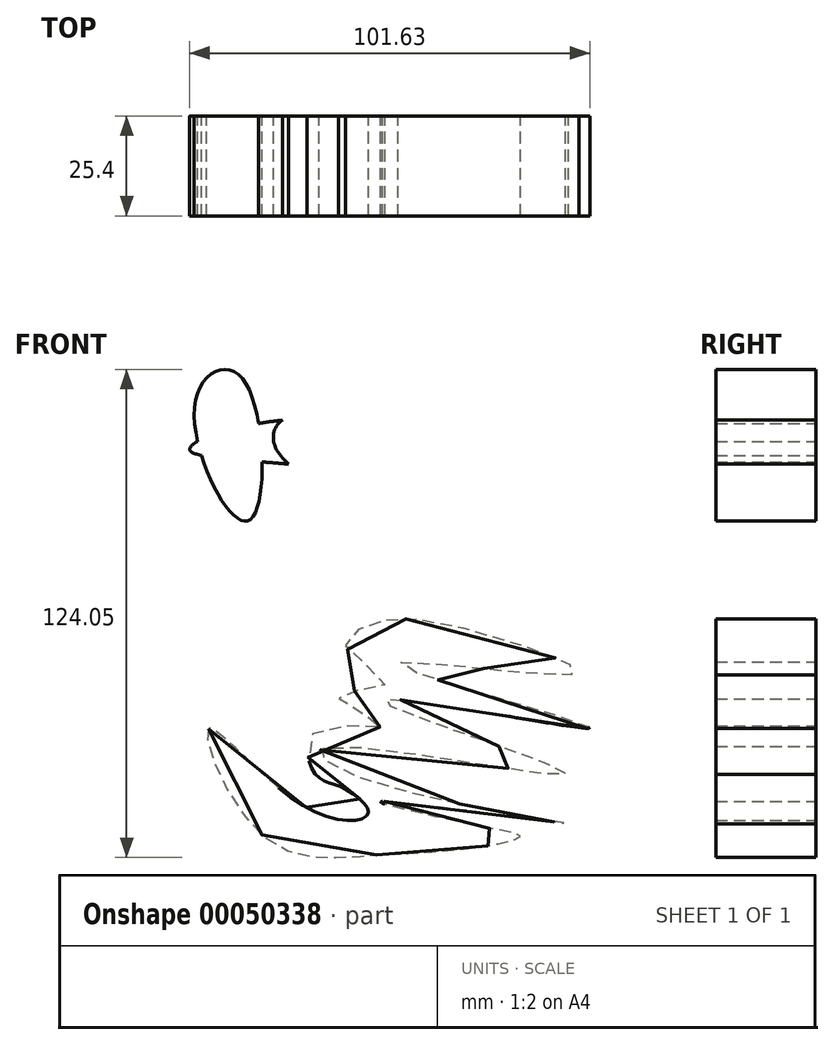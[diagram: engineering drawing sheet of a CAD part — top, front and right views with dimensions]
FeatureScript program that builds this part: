
annotation { "Feature Type Name" : "Feature", "Feature Type Description" : "" }
export const myFeature = defineFeature(function(context is Context, id is Id, definition is map)
    precondition{}
    {
        {
            var Q0;
            Q0=qCreatedBy(makeId("Front.planeOp"),FACE);
            var sketch = newSketch(context, id + "F0", { "sketchPlane" : qUnion([Q0])});
            skFitSpline(sketch, "E0", {"points": [v(-38.95, 44.14) * mm, v(-52.4, 30.13) * mm, v(-46.24, 18.64) * mm, v(-22.7, 8.83) * mm, v(-41.2, -16.4) * mm, v(-37.55, 3.5) * mm, v(-58.01, 19.2) * mm, v(-42.6, 47.78) * mm, v(4.2, 29) * mm, v(-38.95, 44.14) * mm]});
            skFitSpline(sketch, "E1", {"points": [v(-37, 37.7) * mm, v(12.05, 19.48) * mm, v(-21.58, 17.52) * mm, v(-35.87, 21.16) * mm, v(-42.04, 28.73) * mm, v(-37, 37.7) * mm]});
            skFitSpline(sketch, "E2", {"points": [v(-26.9, 30.13) * mm, v(-28.87, 32.93) * mm, v(-28.87, 21.44) * mm, v(-19.34, 20.88) * mm, v(-26.9, 30.13) * mm]});
            skFitSpline(sketch, "E3", {"points": [v(-7.58, 22.84) * mm, v(-17.94, 30.13) * mm, v(-10.66, 19.76) * mm, v(-7.58, 22.84) * mm]});
            skFitSpline(sketch, "E4", {"points": [v(-51.25, -20.84) * mm, v(-38.38, -47.16) * mm, v(-10.66, -53.04) * mm, v(15.94, -51.08) * mm, v(27.98, -48.28) * mm, v(21.54, -46.32) * mm, v(-7.3, -39.32) * mm, v(40.02, -44.92) * mm, v(-14.58, -32.6) * mm, v(-21.58, -25.6) * mm, v(39.46, -32.04) * mm, v(-7.02, -13.56) * mm, v(45.62, -20.56) * mm, v(-3.1, -4.32) * mm, v(42.26, -6.84) * mm, v(10.34, 5.48) * mm, v(-10.66, 5.48) * mm, v(-16.26, 0) * mm, v(-6.46, -9.64) * mm, v(-18.22, -12.44) * mm, v(-7.3, -20) * mm, v(-23.82, -21.4) * mm, v(-24.1, -32.32) * mm, v(-17.38, -35.68) * mm, v(-10.66, -42.12) * mm, v(-25.5, -41.28) * mm, v(-51.25, -20.84) * mm]});
            skSolve(sketch);
        }
        {
            var Q0;
            Q0=makeQuery(id+"F0.imprint","IMPRINT",FACE,{"disambiguationData":[TD([[makeQuery(id+"F0.imprint","IMPRINT",EDGE,{"derivedFrom":sQuery(id+"F0.wireOp",EDGE,"E4")}),1.0]])]});
            extrude(context, id + "F1", {"entities" : qUnion([Q0]), "depth" : 25.4 * mm});
        }
        {
            var Q0;
            Q0=qCreatedBy(makeId("Front.planeOp"),FACE);
            var sketch = newSketch(context, id + "F2", { "sketchPlane" : qUnion([Q0])});
            skFitSpline(sketch, "E5", {"points": [v(-56.01, 50.28) * mm, v(-7.3, 57) * mm, v(41.42, 32.36) * mm, v(-8.42, 43.56) * mm, v(-56.01, 50.28) * mm]});
            skFitSpline(sketch, "E6", {"points": [v(-30.9, 46.44) * mm, v(-32.47, 57.6) * mm, v(0, 52.52) * mm, v(0, 41.84) * mm, v(-30.9, 46.44) * mm]});
            skSolve(sketch);
        }
        {
            var Q0;
            {var subQ0=sQuery(id+"F2.wireOp",EDGE,"E6");var subQ1=sQuery(id+"F2.wireOp",EDGE,"E5");var subQ2=makeQuery(id+"F2.imprint","INTERSECT",VERTEX,{"disambiguationData":[OD(1.0)],"derivedFrom":[subQ1,subQ0]});Q0=makeQuery(id+"F2.imprint","IMPRINT",FACE,{"disambiguationData":[TD([[makeQuery(id+"F2.imprint","IMPRINT",EDGE,{"disambiguationData":[TD([[subQ2,1.0]])],"derivedFrom":subQ1}),-1.0]])]});}
            extrude(context, id + "F3", {"entities" : qUnion([Q0]), "depth" : 25.4 * mm});
        }
        {
            var Q0;
            Q0=qCreatedBy(makeId("Front.planeOp"),FACE);
            var sketch = newSketch(context, id + "F4", { "sketchPlane" : qUnion([Q0])});
            skFitSpline(sketch, "E7", {"points": [v(-54.61, 62.31) * mm, v(-41.18, 32.08) * mm, v(-43.13, 68.75) * mm, v(-54.61, 62.31) * mm]});
            skSolve(sketch);
        }
        {
            var Q0;
            Q0=makeQuery(id+"F4.imprint","IMPRINT",FACE,{"disambiguationData":[TD([[makeQuery(id+"F4.imprint","IMPRINT",EDGE,{"derivedFrom":sQuery(id+"F4.wireOp",EDGE,"E7")}),1.0]])]});
            extrude(context, id + "F5", {"entities" : qUnion([Q0]), "operationType" : NewBodyOperationType.ADD, "depth" : 25.4 * mm});
        }
    });
